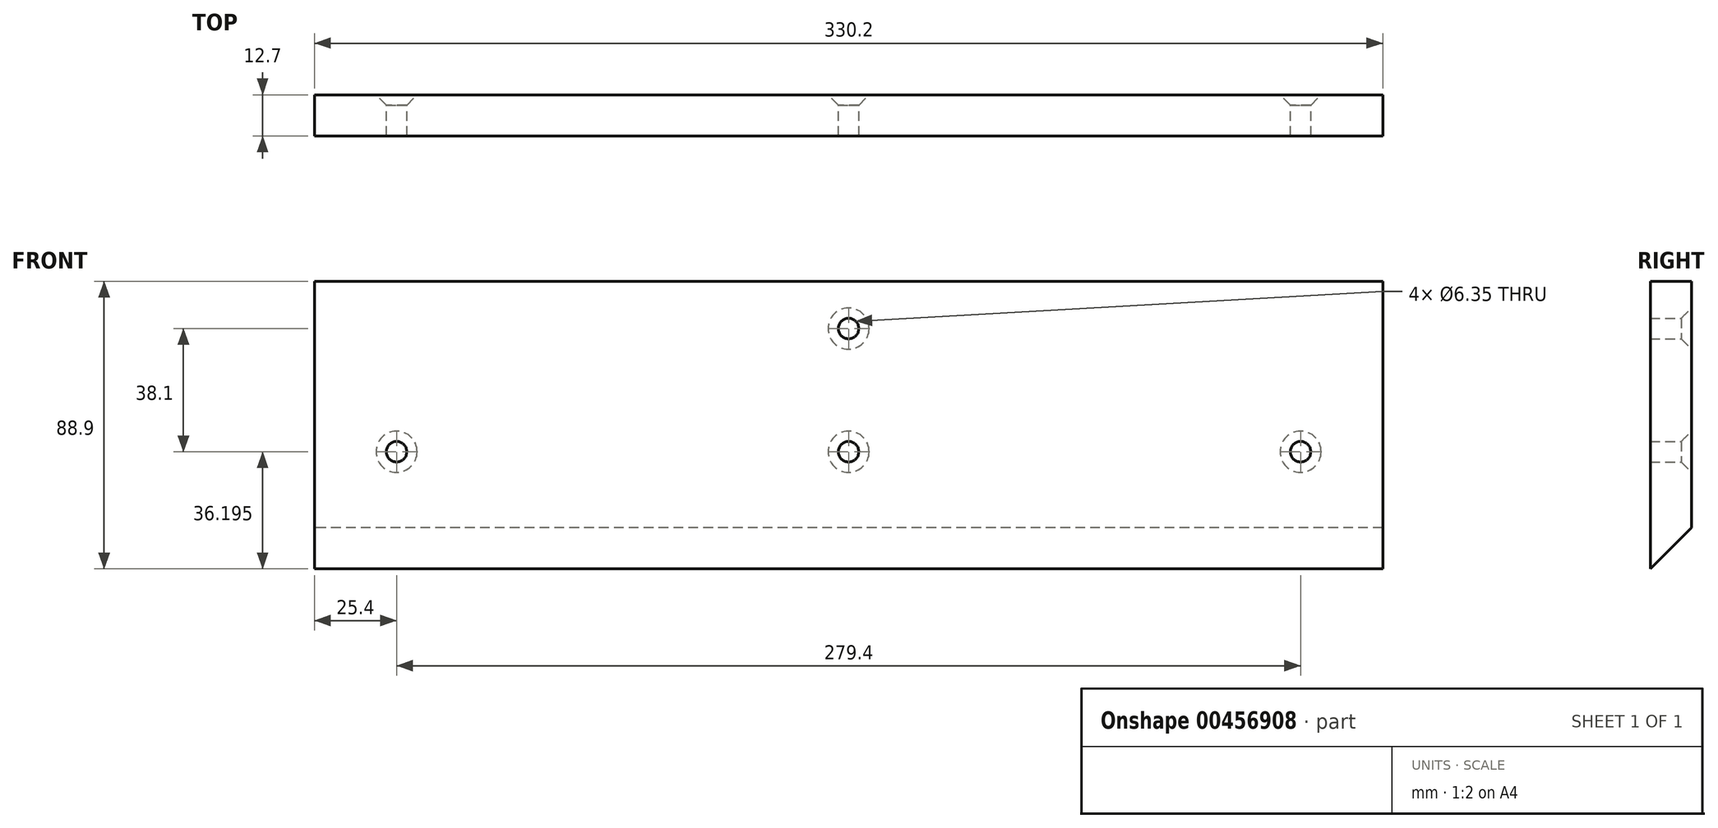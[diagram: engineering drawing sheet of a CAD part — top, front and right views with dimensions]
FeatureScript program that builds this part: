
annotation { "Feature Type Name" : "Feature", "Feature Type Description" : "" }
export const myFeature = defineFeature(function(context is Context, id is Id, definition is map)
    precondition{}
    {
        {
            var Q0;
            Q0=qCreatedBy(makeId("Right.planeOp"),FACE);
            var sketch = newSketch(context, id + "F0", { "sketchPlane" : qUnion([Q0])});
            skLineSegment(sketch, "E0.bottom", {"start": v(-141.46, 88.9) * mm, "end": v(-128.76, 88.9) * mm});
            skLineSegment(sketch, "E1", {"start": v(-141.46, 0) * mm, "end": v(-128.76, 12.7) * mm});
            skLineSegment(sketch, "E2", {"start": v(-141.46, 88.9) * mm, "end": v(-141.46, 0) * mm});
            skLineSegment(sketch, "E3", {"start": v(-128.76, 88.9) * mm, "end": v(-128.76, 12.7) * mm});
            skSolve(sketch);
        }
        {
            var Q0;
            Q0=makeQuery(id+"F0.imprint","IMPRINT",FACE,{"disambiguationData":[TD([[makeQuery(id+"F0.imprint","IMPRINT",EDGE,{"derivedFrom":sQuery(id+"F0.wireOp",EDGE,"E0.bottom")}),-1.0]])]});
            extrude(context, id + "F1", {"entities" : qUnion([Q0]), "depth" : 330.2 * mm});
        }
        {
            var Q0;
            {var subQ0=sQuery(id+"F0.wireOp",EDGE,"E3");Q0=makeQuery(id+"FpvZI3BrmpHNNxv_1.boolean.opBoolean","MERGE",FACE,{"derivedFrom":[makeQuery(id+"F1.opExtrude","SWEPT_FACE",FACE,{"disambiguationData":[OSD([subQ0])]}),makeQuery(id+"FpvZI3BrmpHNNxv_1.opExtrude","CAP_FACE",FACE,{"disambiguationData":[OSD([sQuery(id+"F0.wireOp",EDGE,"E0.bottom"),subQ0,sQuery(id+"FzDqwvfrmprKgJQ_1.wireOp",EDGE,"1nV9llzo-cz9i-70ST-YEmF-xcA2EYtzIXPg"),sQuery(id+"FzDqwvfrmprKgJQ_1.wireOp",EDGE,"j2RhicXh-JIYP-Fch2-HXI4-wMuu1fK2muzb"),sQuery(id+"FzDqwvfrmprKgJQ_1.wireOp",EDGE,"jaiMSpug-MQjc-XQqv-KiCT-kCt3Hkm3jDX7")])],"isStart":true})]});}
            var sketch = newSketch(context, id + "F2", { "sketchPlane" : qUnion([Q0])});
            skPoint(sketch, "E4", {"position": v(-165.1, 74.3) * mm});
            skPoint(sketch, "E5", {"position": v(-165.1, 36.2) * mm});
            skPoint(sketch, "E6", {"position": v(-304.8, 36.2) * mm});
            skPoint(sketch, "E7", {"position": v(-25.4, 36.2) * mm});
            skPoint(sketch, "E8", {"position": v(-165.1, 12.7) * mm});
            skPoint(sketch, "E9", {"position": v(0, 50.8) * mm});
            skPoint(sketch, "E10", {"position": v(38.1, 36.2) * mm});
            skPoint(sketch, "E11", {"position": v(-431.8, 36.2) * mm});
            skPoint(sketch, "E12", {"position": v(-368.3, 36.2) * mm});
            skSolve(sketch);
        }
        {
            var Q0;
            Q0=sQuery(id+"F2.wireOp",VERTEX,"E5");
            var Q1;
            Q1=sQuery(id+"F2.wireOp",VERTEX,"E4");
            var Q2;
            Q2=sQuery(id+"F2.wireOp",VERTEX,"E6");
            var Q3;
            Q3=sQuery(id+"F2.wireOp",VERTEX,"E7");
            var Q4;
            Q4=sQuery(id+"F2.wireOp",VERTEX,"E10");
            var Q5;
            Q5=sQuery(id+"F2.wireOp",VERTEX,"E11");
            var Q6;
            Q6=sQuery(id+"F2.wireOp",VERTEX,"E12");
            var Q7;
            Q7=sQuery(id+"F2.wireOp",VERTEX,"E10");
            var Q8;
            Q8=makeQuery(id+"F1.opExtrude","SWEPT_BODY",BODY,{"disambiguationData":[OSD([sQuery(id+"F0.wireOp",EDGE,"E0.bottom"),sQuery(id+"F0.wireOp",EDGE,"E1"),sQuery(id+"F0.wireOp",EDGE,"E2"),sQuery(id+"F0.wireOp",EDGE,"E3")])]});
            hole(context, id + "F3", {"style" : HoleStyle.C_SINK, "endStyle" : HoleEndStyle.THROUGH, "holeDiameter" : 6.35 * mm, "cSinkDiameter" : 12.7 * mm, "cSinkAngle" : 90 * degree, "isTappedThrough" : true, "tappedDepth" : 12.7 * mm, "tapClearance" : 3, "locations" : qUnion([Q0, Q1, Q2, Q3, Q4, Q5, Q6, Q7]), "scope" : qUnion([Q8])});
        }
    });
